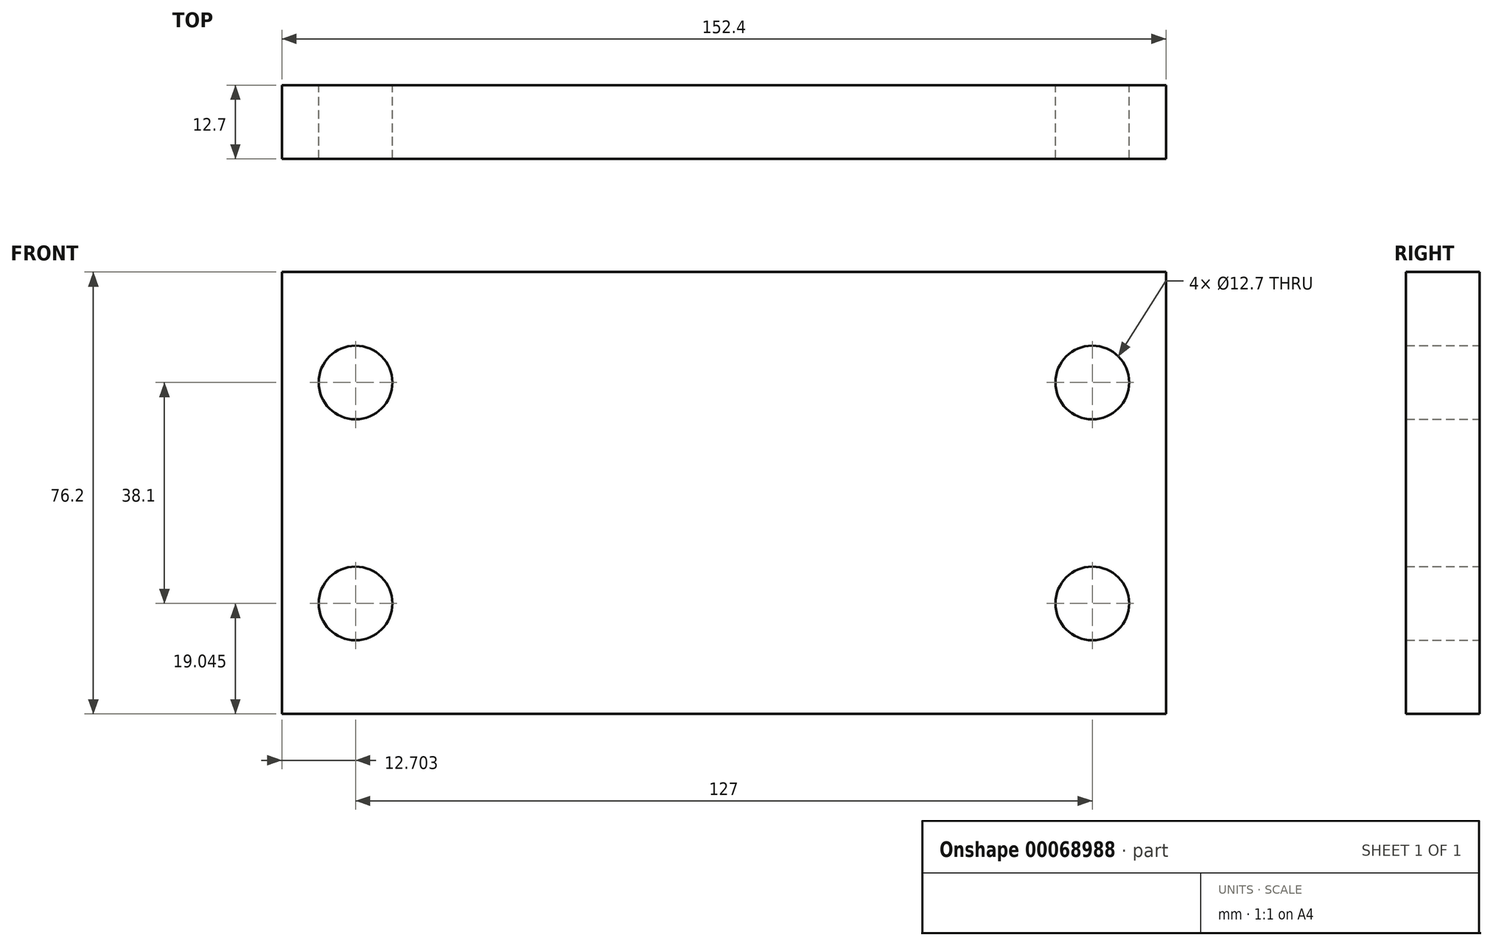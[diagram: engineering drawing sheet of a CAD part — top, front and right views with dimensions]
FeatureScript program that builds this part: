
annotation { "Feature Type Name" : "Feature", "Feature Type Description" : "" }
export const myFeature = defineFeature(function(context is Context, id is Id, definition is map)
    precondition{}
    {
        {
            var Q0;
            Q0=qCreatedBy(makeId("Front.planeOp"),FACE);
            var sketch = newSketch(context, id + "F0", { "sketchPlane" : qUnion([Q0])});
            skLineSegment(sketch, "E0", {"start": v(-76.54, 38) * mm, "end": v(75.86, 38) * mm});
            skLineSegment(sketch, "E1", {"start": v(-76.54, -38.2) * mm, "end": v(-76.81, -38.2) * mm});
            skLineSegment(sketch, "E2", {"start": v(-76.54, 38) * mm, "end": v(-76.54, -38.2) * mm});
            skLineSegment(sketch, "E3", {"start": v(75.86, 38) * mm, "end": v(75.86, -38.2) * mm});
            skLineSegment(sketch, "E4", {"start": v(-0.34, 38) * mm, "end": v(-0.34, -38.2) * mm, "construction": true});
            skCircle(sketch, "E5", {"center": v(63.16, 18.96) * mm, "radius": 6.35 * mm});
            skCircle(sketch, "E6.MirrorC", {"center": v(-63.84, 18.96) * mm, "radius": 6.35 * mm});
            skLineSegment(sketch, "E7", {"start": v(-76.54, -0.1) * mm, "end": v(75.86, -0.1) * mm});
            skCircle(sketch, "E8.MirrorC", {"center": v(-63.84, -19.14) * mm, "radius": 6.35 * mm});
            skCircle(sketch, "E9.MirrorC", {"center": v(63.16, -19.14) * mm, "radius": 6.35 * mm});
            skPoint(sketch, "E10.orphan", {"position": v(75.59, -38.2) * mm});
            skLineSegment(sketch, "E11", {"start": v(-76.54, -38.2) * mm, "end": v(-0.34, -38.2) * mm});
            skLineSegment(sketch, "E12", {"start": v(-0.34, -38.2) * mm, "end": v(75.86, -38.2) * mm});
            skSolve(sketch);
        }
        {
            var Q0;
            {var subQ1=sQuery(id+"F0.wireOp",EDGE,"E0");Q0=makeQuery(id+"F0.imprint","IMPRINT",FACE,{"disambiguationData":[TD([[makeQuery(id+"F0.imprint","IMPRINT",EDGE,{"derivedFrom":subQ1}),-1.0]])]});}
            extrude(context, id + "F1", {"entities" : qUnion([Q0]), "depth" : 12.7 * mm});
        }
        {
            var Q0;
            {var subQ0=sQuery(id+"F0.wireOp",EDGE,"E7");Q0=makeQuery(id+"F0.imprint","IMPRINT",FACE,{"disambiguationData":[TD([[makeQuery(id+"F0.imprint","IMPRINT",EDGE,{"derivedFrom":subQ0}),-1.0]])]});}
            extrude(context, id + "F2", {"entities" : qUnion([Q0]), "operationType" : NewBodyOperationType.ADD, "depth" : 12.7 * mm});
        }
    });
